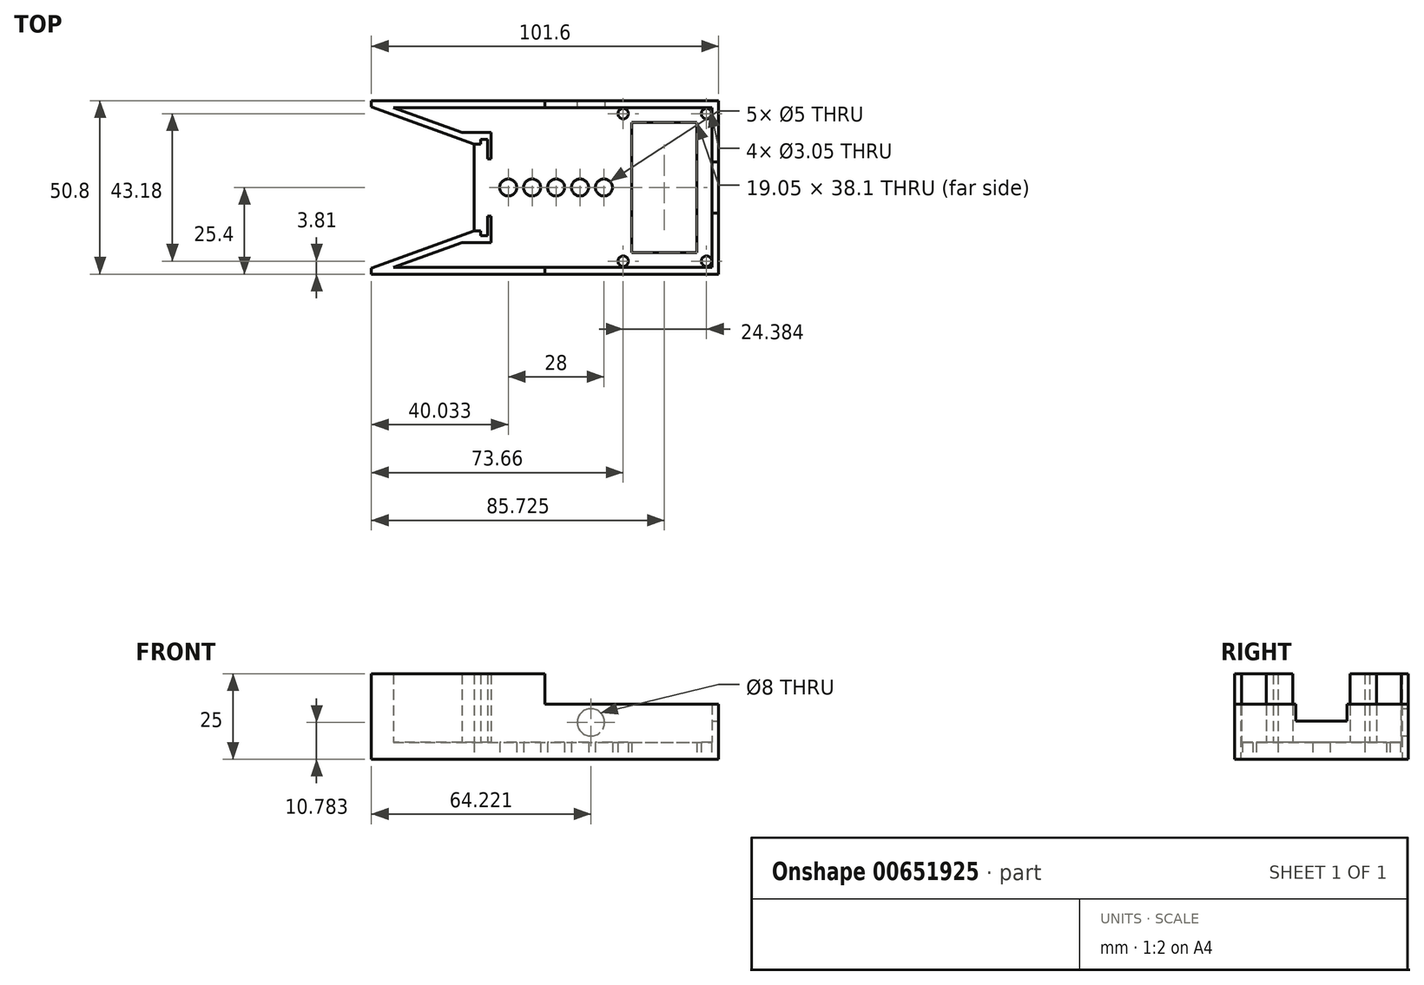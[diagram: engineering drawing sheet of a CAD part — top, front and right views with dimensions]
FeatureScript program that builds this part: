
annotation { "Feature Type Name" : "Feature", "Feature Type Description" : "" }
export const myFeature = defineFeature(function(context is Context, id is Id, definition is map)
    precondition{}
    {
        {
            var Q0;
            Q0=qCreatedBy(makeId("Top.planeOp"),FACE);
            var sketch = newSketch(context, id + "F0", { "sketchPlane" : qUnion([Q0])});
            skLineSegment(sketch, "E0.bottom", {"start": v(-50.8, 25.4) * mm, "end": v(50.8, 25.4) * mm});
            skLineSegment(sketch, "E0.top", {"start": v(-50.8, -25.4) * mm, "end": v(50.8, -25.4) * mm});
            skLineSegment(sketch, "E0.left", {"start": v(-50.8, 25.4) * mm, "end": v(-50.8, 23.62) * mm});
            skLineSegment(sketch, "E0.right", {"start": v(50.8, 25.4) * mm, "end": v(50.8, -25.4) * mm});
            skLineSegment(sketch, "E1.0", {"start": v(44.45, 19.05) * mm, "end": v(44.45, -19.05) * mm});
            skLineSegment(sketch, "E2.0", {"start": v(25.4, 19.05) * mm, "end": v(44.45, 19.05) * mm});
            skLineSegment(sketch, "E3.0", {"start": v(25.4, -19.05) * mm, "end": v(44.45, -19.05) * mm});
            skLineSegment(sketch, "E4.0", {"start": v(25.4, 19.05) * mm, "end": v(25.4, -19.05) * mm});
            skLineSegment(sketch, "E5", {"start": v(-20.8, 12.7) * mm, "end": v(-20.8, -12.7) * mm});
            skLineSegment(sketch, "E6", {"start": v(-20.8, -12.7) * mm, "end": v(-50.8, -23.62) * mm});
            skLineSegment(sketch, "E7.MirrorCS", {"start": v(-20.8, 12.7) * mm, "end": v(-50.8, 23.62) * mm});
            skLineSegment(sketch, "E8.trimOffspring", {"start": v(-50.8, -23.62) * mm, "end": v(-50.8, -25.4) * mm});
            skPoint(sketch, "E9.start.orphan", {"position": v(-50.8, 0) * mm});
            skCircle(sketch, "E10", {"center": v(17.23, 0) * mm, "radius": 2.5 * mm});
            skCircle(sketch, "E11.1.0.0", {"center": v(10.23, 0) * mm, "radius": 2.5 * mm});
            skCircle(sketch, "E11.2.0.0", {"center": v(3.23, 0) * mm, "radius": 2.5 * mm});
            skCircle(sketch, "E11.3.0.0", {"center": v(-3.77, 0) * mm, "radius": 2.5 * mm});
            skCircle(sketch, "E11.4.0.0", {"center": v(-10.77, 0) * mm, "radius": 2.5 * mm});
            skLineSegment(sketch, "E11.direction1", {"start": v(17.23, 0) * mm, "end": v(10.23, 0) * mm, "construction": true});
            skCircle(sketch, "E12", {"center": v(22.86, -21.6) * mm, "radius": 1.52 * mm});
            skCircle(sketch, "E13.0.1.0", {"center": v(22.86, 21.59) * mm, "radius": 1.52 * mm});
            skCircle(sketch, "E13.1.0.0", {"center": v(47.24, -21.6) * mm, "radius": 1.52 * mm});
            skCircle(sketch, "E13.1.1.0", {"center": v(47.24, 21.59) * mm, "radius": 1.52 * mm});
            skSolve(sketch);
        }
        {
            var Q0;
            Q0=makeQuery(id+"F0.imprint","IMPRINT",FACE,{"disambiguationData":[TD([[makeQuery(id+"F0.imprint","IMPRINT",EDGE,{"derivedFrom":sQuery(id+"F0.wireOp",EDGE,"E0.bottom")}),-1.0]])]});
            extrude(context, id + "F1", {"entities" : qUnion([Q0]), "depth" : 5 * mm, "offsetDistance" : 25.4 * mm});
        }
        {
            var Q0;
            Q0=makeQuery(id+"F1.opExtrude","CAP_FACE",FACE,{"disambiguationData":[OSD([sQuery(id+"F0.wireOp",EDGE,"E0.bottom"),sQuery(id+"F0.wireOp",EDGE,"E0.top"),sQuery(id+"F0.wireOp",EDGE,"E0.left"),sQuery(id+"F0.wireOp",EDGE,"E0.right"),sQuery(id+"F0.wireOp",EDGE,"E1.0"),sQuery(id+"F0.wireOp",EDGE,"E2.0"),sQuery(id+"F0.wireOp",EDGE,"E3.0"),sQuery(id+"F0.wireOp",EDGE,"E4.0"),sQuery(id+"F0.wireOp",EDGE,"E5"),sQuery(id+"F0.wireOp",EDGE,"E6"),sQuery(id+"F0.wireOp",EDGE,"E7.MirrorCS"),sQuery(id+"F0.wireOp",EDGE,"E8.trimOffspring"),sQuery(id+"F0.wireOp",EDGE,"E10"),sQuery(id+"F0.wireOp",EDGE,"E11.1.0.0"),sQuery(id+"F0.wireOp",EDGE,"E11.2.0.0"),sQuery(id+"F0.wireOp",EDGE,"E11.3.0.0"),sQuery(id+"F0.wireOp",EDGE,"E11.4.0.0")])],"isStart":false});
            var sketch = newSketch(context, id + "F2", { "sketchPlane" : qUnion([Q0])});
            skLineSegment(sketch, "E14", {"start": v(50.8, 25.4) * mm, "end": v(50.8, -25.4) * mm});
            skLineSegment(sketch, "E15", {"start": v(50.8, -25.4) * mm, "end": v(-50.8, -25.4) * mm});
            skLineSegment(sketch, "E16", {"start": v(-50.8, -25.4) * mm, "end": v(-50.8, -23.62) * mm});
            skLineSegment(sketch, "E17", {"start": v(-50.8, -23.62) * mm, "end": v(-20.8, -12.7) * mm});
            skLineSegment(sketch, "E18", {"start": v(-20.8, 12.7) * mm, "end": v(-50.8, 23.62) * mm});
            skLineSegment(sketch, "E19", {"start": v(-50.8, 23.62) * mm, "end": v(-50.8, 25.4) * mm});
            skLineSegment(sketch, "E20.0", {"start": v(-18.8, 14.1) * mm, "end": v(-18.8, 12.7) * mm});
            skLineSegment(sketch, "E20.1", {"start": v(-44.35, -23.4) * mm, "end": v(48.8, -23.4) * mm});
            skLineSegment(sketch, "E20.2", {"start": v(48.8, -23.4) * mm, "end": v(48.8, 23.4) * mm});
            skLineSegment(sketch, "E20.3", {"start": v(-24.3, -16.1) * mm, "end": v(-44.35, -23.4) * mm});
            skLineSegment(sketch, "E20.4", {"start": v(48.8, 23.4) * mm, "end": v(-44.35, 23.4) * mm});
            skLineSegment(sketch, "E20.5", {"start": v(-44.35, 23.4) * mm, "end": v(-24.3, 16.1) * mm});
            skLineSegment(sketch, "E21", {"start": v(-20.8, 12.7) * mm, "end": v(-18.8, 12.7) * mm});
            skLineSegment(sketch, "E22", {"start": v(-20.8, -12.7) * mm, "end": v(-18.8, -12.7) * mm});
            skLineSegment(sketch, "E23.trimOffspring", {"start": v(-18.8, -12.7) * mm, "end": v(-18.8, -14.1) * mm});
            skLineSegment(sketch, "E24", {"start": v(-18.8, 14.1) * mm, "end": v(-16.8, 14.1) * mm});
            skLineSegment(sketch, "E25", {"start": v(-16.8, 14.1) * mm, "end": v(-16.8, 8.37) * mm});
            skLineSegment(sketch, "E26", {"start": v(-16.8, -14.1) * mm, "end": v(-18.8, -14.1) * mm});
            skLineSegment(sketch, "E27", {"start": v(-15.8, 14.1) * mm, "end": v(-15.8, 8.37) * mm});
            skLineSegment(sketch, "E28", {"start": v(-15.8, 14.1) * mm, "end": v(-15.8, 16.1) * mm});
            skLineSegment(sketch, "E29", {"start": v(-15.8, 16.1) * mm, "end": v(-24.3, 16.1) * mm});
            skLineSegment(sketch, "E30.MirrorCS", {"start": v(-15.8, -16.1) * mm, "end": v(-24.3, -16.1) * mm});
            skLineSegment(sketch, "E31.MirrorCS", {"start": v(-15.8, -14.1) * mm, "end": v(-15.8, -16.1) * mm});
            skLineSegment(sketch, "E32", {"start": v(-16.8, 8.37) * mm, "end": v(-15.8, 8.37) * mm});
            skLineSegment(sketch, "E33.MirrorCS", {"start": v(-16.8, -8.37) * mm, "end": v(-15.8, -8.37) * mm});
            skLineSegment(sketch, "E34.trimOffspring", {"start": v(-16.8, -8.37) * mm, "end": v(-16.8, -14.1) * mm});
            skLineSegment(sketch, "E35.trimOffspring", {"start": v(-15.8, -8.37) * mm, "end": v(-15.8, -14.1) * mm});
            skSolve(sketch);
        }
        {
            var Q0;
            Q0=makeQuery(id+"F2.imprint","IMPRINT",FACE,{"disambiguationData":[TD([[makeQuery(id+"F2.imprint","IMPRINT",EDGE,{"derivedFrom":sQuery(id+"F2.wireOp",EDGE,"E14")}),-1.0]])]});
            extrude(context, id + "F3", {"entities" : qUnion([Q0]), "operationType" : NewBodyOperationType.ADD, "depth" : 20 * mm, "offsetDistance" : 25.4 * mm});
        }
        {
            var Q0;
            Q0=makeQuery(id+"F3.opExtrude","SWEPT_FACE",FACE,{"disambiguationData":[OSD([sQuery(id+"F2.wireOp",EDGE,"E20.4")])]});
            var sketch = newSketch(context, id + "F4", { "sketchPlane" : qUnion([Q0])});
            skCircle(sketch, "E36", {"center": v(13.42, 10.78) * mm, "radius": 4 * mm});
            skSolve(sketch);
        }
        {
            var Q0;
            Q0=makeQuery(id+"F4.imprint","IMPRINT",FACE,{"disambiguationData":[TD([[makeQuery(id+"F4.imprint","IMPRINT",EDGE,{"derivedFrom":sQuery(id+"F4.wireOp",EDGE,"E36")}),1.0]])]});
            extrude(context, id + "F5", {"entities" : qUnion([Q0]), "operationType" : NewBodyOperationType.REMOVE, "oppositeDirection" : true, "depth" : 25.4 * mm, "offsetDistance" : 25.4 * mm});
        }
        {
            var Q0;
            Q0=makeQuery(id+"F3.opExtrude","CAP_FACE",FACE,{"disambiguationData":[OSD([sQuery(id+"F0.wireOp",EDGE,"E0.bottom"),sQuery(id+"F2.wireOp",EDGE,"E14"),sQuery(id+"F2.wireOp",EDGE,"E15"),sQuery(id+"F2.wireOp",EDGE,"E16"),sQuery(id+"F2.wireOp",EDGE,"E17"),sQuery(id+"F2.wireOp",EDGE,"E18"),sQuery(id+"F2.wireOp",EDGE,"E19"),sQuery(id+"F2.wireOp",EDGE,"E20.0"),sQuery(id+"F2.wireOp",EDGE,"E20.1"),sQuery(id+"F2.wireOp",EDGE,"E20.2"),sQuery(id+"F2.wireOp",EDGE,"E20.3"),sQuery(id+"F2.wireOp",EDGE,"E20.4"),sQuery(id+"F2.wireOp",EDGE,"E20.5"),sQuery(id+"F2.wireOp",EDGE,"E21"),sQuery(id+"F2.wireOp",EDGE,"E22"),sQuery(id+"F2.wireOp",EDGE,"E23.trimOffspring"),sQuery(id+"F2.wireOp",EDGE,"E24"),sQuery(id+"F2.wireOp",EDGE,"E25"),sQuery(id+"F2.wireOp",EDGE,"E26"),sQuery(id+"F2.wireOp",EDGE,"E27"),sQuery(id+"F2.wireOp",EDGE,"E28"),sQuery(id+"F2.wireOp",EDGE,"E29"),sQuery(id+"F2.wireOp",EDGE,"E30.MirrorCS"),sQuery(id+"F2.wireOp",EDGE,"E31.MirrorCS"),sQuery(id+"F2.wireOp",EDGE,"E32"),sQuery(id+"F2.wireOp",EDGE,"E33.MirrorCS"),sQuery(id+"F2.wireOp",EDGE,"E34.trimOffspring"),sQuery(id+"F2.wireOp",EDGE,"E35.trimOffspring")])],"isStart":false});
            var sketch = newSketch(context, id + "F6", { "sketchPlane" : qUnion([Q0])});
            skLineSegment(sketch, "E37.bottom", {"start": v(50.8, 25.4) * mm, "end": v(0, 25.4) * mm});
            skLineSegment(sketch, "E37.top", {"start": v(50.8, -25.4) * mm, "end": v(0, -25.4) * mm});
            skLineSegment(sketch, "E37.left", {"start": v(50.8, 25.4) * mm, "end": v(50.8, -25.4) * mm});
            skLineSegment(sketch, "E37.right", {"start": v(0, 25.4) * mm, "end": v(0, -25.4) * mm});
            skSolve(sketch);
        }
        {
            var Q0;
            Q0 = qSketchRegion(id + "F6", true);
            extrude(context, id + "F7", {"entities" : qUnion([Q0]), "operationType" : NewBodyOperationType.REMOVE, "oppositeDirection" : true, "depth" : 8.9 * mm, "offsetDistance" : 25.4 * mm});
        }
        {
            var Q0;
            Q0=makeQuery(id+"F3.boolean.opBoolean","MERGE",FACE,{"derivedFrom":[makeQuery(id+"F1.opExtrude","SWEPT_FACE",FACE,{"disambiguationData":[OSD([sQuery(id+"F0.wireOp",EDGE,"E0.right")])]}),makeQuery(id+"F3.opExtrude","SWEPT_FACE",FACE,{"disambiguationData":[OSD([sQuery(id+"F2.wireOp",EDGE,"E14")])]})]});
            var sketch = newSketch(context, id + "F8", { "sketchPlane" : qUnion([Q0])});
            skPoint(sketch, "E38.startSnap0", {"position": v(0, 0) * mm});
            skLineSegment(sketch, "E39", {"start": v(-7.5, 11.17) * mm, "end": v(7.5, 11.17) * mm});
            skLineSegment(sketch, "E40", {"start": v(-7.5, 11.17) * mm, "end": v(-7.5, 16.1) * mm});
            skLineSegment(sketch, "E41", {"start": v(-7.5, 16.1) * mm, "end": v(7.5, 16.1) * mm});
            skLineSegment(sketch, "E42", {"start": v(7.5, 16.1) * mm, "end": v(7.5, 11.17) * mm});
            skSolve(sketch);
        }
        {
            var Q0;
            Q0 = qSketchRegion(id + "F8", true);
            extrude(context, id + "F9", {"entities" : qUnion([Q0]), "operationType" : NewBodyOperationType.REMOVE, "oppositeDirection" : true, "depth" : 25.4 * mm, "offsetDistance" : 25.4 * mm});
        }
    });
